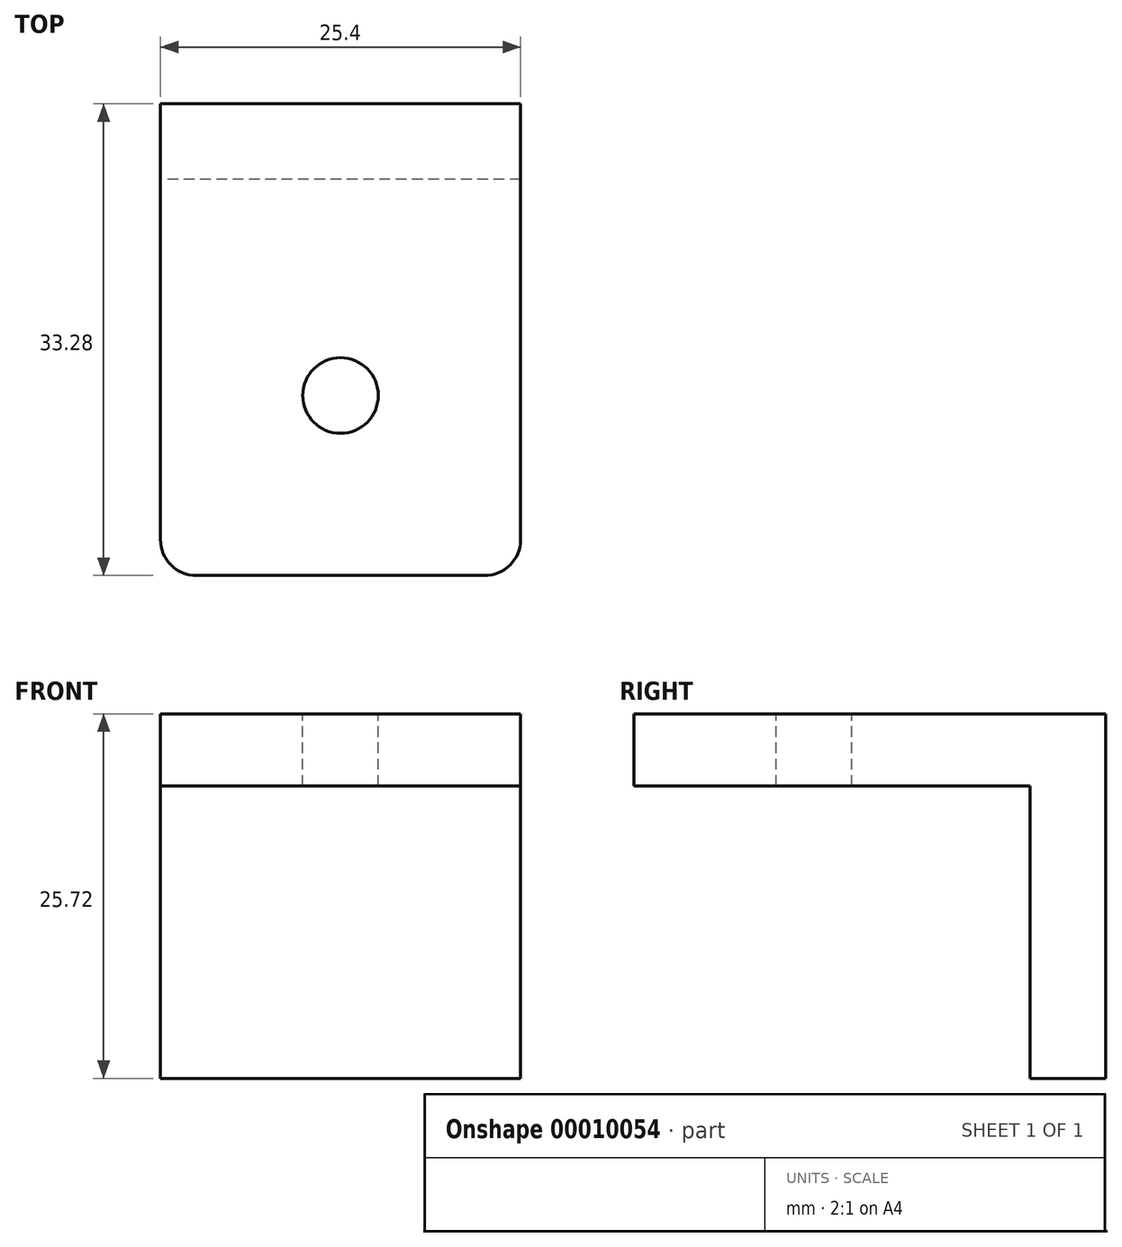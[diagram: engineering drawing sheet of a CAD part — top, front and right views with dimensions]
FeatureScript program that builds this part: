
annotation { "Feature Type Name" : "Feature", "Feature Type Description" : "" }
export const myFeature = defineFeature(function(context is Context, id is Id, definition is map)
    precondition{}
    {
        {
            var Q0;
            Q0=qCreatedBy(makeId("Top.planeOp"),FACE);
            var sketch = newSketch(context, id + "F0", { "sketchPlane" : qUnion([Q0])});
            skLineSegment(sketch, "E0.bottom", {"start": v(-12.7, 3.04) * mm, "end": v(12.7, 3.04) * mm});
            skLineSegment(sketch, "E0.top", {"start": v(-10.16, -30.24) * mm, "end": v(10.16, -30.24) * mm});
            skLineSegment(sketch, "E0.left", {"start": v(-12.7, 3.04) * mm, "end": v(-12.7, -27.7) * mm});
            skLineSegment(sketch, "E0.right", {"start": v(12.7, 3.04) * mm, "end": v(12.7, -27.7) * mm});
            skCircle(sketch, "E1", {"center": v(0, -17.54) * mm, "radius": 2.67 * mm});
            skLineSegment(sketch, "E2", {"start": v(-12.7, -2.3) * mm, "end": v(12.7, -2.3) * mm});
            skPoint(sketch, "E3.visualSharp", {"position": v(-12.7, -30.24) * mm});
            skArc(sketch, "E3.filletArc", {"start": v(-12.7, -27.7) * mm, "mid": v(-11.96, -29.5) * mm, "end": v(-10.16, -30.24) * mm});
            skPoint(sketch, "E4.visualSharp", {"position": v(12.7, -30.24) * mm});
            skArc(sketch, "E4.filletArc", {"start": v(10.16, -30.24) * mm, "mid": v(11.96, -29.5) * mm, "end": v(12.7, -27.7) * mm});
            skSolve(sketch);
        }
        {
            var Q0;
            {var subQ2=sQuery(id+"F0.wireOp",EDGE,"E0.bottom");Q0=makeQuery(id+"F0.imprint","IMPRINT",FACE,{"disambiguationData":[TD([[makeQuery(id+"F0.imprint","IMPRINT",EDGE,{"derivedFrom":subQ2}),-1.0]])]});}
            var Q1;
            Q1=makeQuery(id+"F0.imprint","IMPRINT",FACE,{"disambiguationData":[TD([[makeQuery(id+"F0.imprint","IMPRINT",EDGE,{"derivedFrom":sQuery(id+"F0.wireOp",EDGE,"E0.top")}),1.0]])]});
            extrude(context, id + "F1", {"entities" : qUnion([Q0, Q1]), "depth" : 5.08 * mm});
        }
        {
            var Q0;
            Q0=makeQuery(id+"F1.opExtrude","CAP_FACE",FACE,{"disambiguationData":[OSD([sQuery(id+"F0.wireOp",EDGE,"E0.bottom"),sQuery(id+"F0.wireOp",EDGE,"E0.top"),sQuery(id+"F0.wireOp",EDGE,"E0.left"),sQuery(id+"F0.wireOp",EDGE,"E0.right"),sQuery(id+"F0.wireOp",EDGE,"E1"),sQuery(id+"F0.wireOp",EDGE,"E3.filletArc"),sQuery(id+"F0.wireOp",EDGE,"E4.filletArc")])],"isStart":false});
            var sketch = newSketch(context, id + "F2", { "sketchPlane" : qUnion([Q0])});
            skLineSegment(sketch, "E5.0", {"start": v(-12.7, 3.04) * mm, "end": v(12.7, 3.04) * mm});
            skLineSegment(sketch, "E5.1", {"start": v(-12.7, 3.04) * mm, "end": v(-12.7, -27.7) * mm});
            skLineSegment(sketch, "E5.2", {"start": v(12.7, 3.04) * mm, "end": v(12.7, -27.7) * mm});
            skLineSegment(sketch, "E6", {"start": v(-12.7, -2.3) * mm, "end": v(12.7, -2.3) * mm});
            skSolve(sketch);
        }
        {
            var Q0;
            {var subQ2=sQuery(id+"F2.wireOp",EDGE,"E5.0");Q0=makeQuery(id+"F2.imprint","IMPRINT",FACE,{"disambiguationData":[TD([[makeQuery(id+"F2.imprint","IMPRINT",EDGE,{"derivedFrom":subQ2}),-1.0]])]});}
            extrude(context, id + "F3", {"entities" : qUnion([Q0]), "operationType" : NewBodyOperationType.ADD, "depth" : 20.64 * mm});
        }
        {
            var Q0;
            Q0=makeQuery(id+"F1.opExtrude","SWEPT_BODY",BODY,{"disambiguationData":[OSD([sQuery(id+"F0.wireOp",EDGE,"E0.bottom"),sQuery(id+"F0.wireOp",EDGE,"E0.top"),sQuery(id+"F0.wireOp",EDGE,"E0.left"),sQuery(id+"F0.wireOp",EDGE,"E0.right"),sQuery(id+"F0.wireOp",EDGE,"E1"),sQuery(id+"F0.wireOp",EDGE,"E3.filletArc"),sQuery(id+"F0.wireOp",EDGE,"E4.filletArc")])]});
            var Q1;
            Q1=makeQuery(id+"F1.opExtrude","CAP_EDGE",EDGE,{"disambiguationData":[OSD([sQuery(id+"F0.wireOp",EDGE,"E0.bottom")])],"isStart":true});
            transform(context, id + "F4", {"entities" : qUnion([Q0]), "transformType" : TransformType.ROTATION, "transformAxis" : qUnion([Q1]), "angle" : 180 * degree, "makeCopy" : false});
        }
        {
            var Q0;
            Q0=makeQuery(id+"F1.opExtrude","SWEPT_BODY",BODY,{"disambiguationData":[OSD([sQuery(id+"F0.wireOp",EDGE,"E0.bottom"),sQuery(id+"F0.wireOp",EDGE,"E0.top"),sQuery(id+"F0.wireOp",EDGE,"E0.left"),sQuery(id+"F0.wireOp",EDGE,"E0.right"),sQuery(id+"F0.wireOp",EDGE,"E1"),sQuery(id+"F0.wireOp",EDGE,"E3.filletArc"),sQuery(id+"F0.wireOp",EDGE,"E4.filletArc")])]});
            var Q1;
            Q1=makeQuery(id+"F3.boolean.opBoolean","MERGE",EDGE,{"derivedFrom":[makeQuery(id+"F1.opExtrude","SWEPT_EDGE",EDGE,{"disambiguationData":[OSD([sQuery(id+"F0.wireOp",EDGE,"E0.bottom"),sQuery(id+"F0.wireOp",EDGE,"E0.left")])]}),makeQuery(id+"F3.opExtrude","SWEPT_EDGE",EDGE,{"disambiguationData":[OSD([sQuery(id+"F2.wireOp",EDGE,"E5.0"),sQuery(id+"F2.wireOp",EDGE,"E5.1")])]})]});
            transform(context, id + "F5", {"entities" : qUnion([Q0]), "transformType" : TransformType.ROTATION, "transformAxis" : qUnion([Q1]), "angle" : 180 * degree, "makeCopy" : false});
        }
    });
